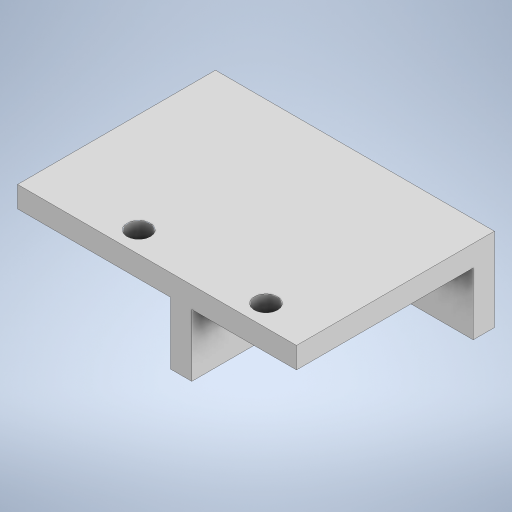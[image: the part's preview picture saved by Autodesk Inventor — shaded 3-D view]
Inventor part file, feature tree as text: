
AUTODESK INVENTOR PART (.ipt)
format: ipt  version: 2023.5 (Build 275446000, 446)  size: 403,968 bytes
history: native  units: in
note: dims shown in document units (in); Inventor stores cm internally (conversion verified against a paired STEP export)
features: extrude x4, sketch x4
ambient origin geometry x8: Origin, YZ Plane, XZ Plane, XY Plane, X Axis, Y Axis, Z Axis, Center Point
bodies: Solid1 (feature_tree)
feature tree (8):
  extrude  "Extrusion1"  Depth=6.8898in
  extrude  "Extrusion2"  TaperAngle=0.0deg  [1 undecoded]
  extrude  "Extrusion3"  Depth=0.1181in
  extrude  "Extrusion4"  Depth=0.3937in
  sketch  "Sketch1"  dims[d0=8.5827in d1=6.8898in]
  sketch  "Sketch2"  dims[d2=1.1024in d3=0.0in]
  sketch  "Sketch3"  dims[d4=1.5748in d5=0.1181in]
  sketch  "Sketch4"  dims[d6=0.1181in d7=1.5748in d8=1.9685in d10=1.6929in d11=1.5748in d13=1.6929in d16=0.9843in d17=0.0in d20=0.1181in d21=0.1299in d22=0.3543in d23=0.1299in d24=0.3543in d25=0.1299in d27=0.3543in d30=0.1181in d31=0.1299in d32=0.3543in d33=0.3937in d34=0.0in d35=0.0in d36=0.0in]
note: 1 required parameter value undecoded (feature->parameter linkage not recoverable at this tier; creation-order binding heuristic only, values carry confidence <= 0.55)
